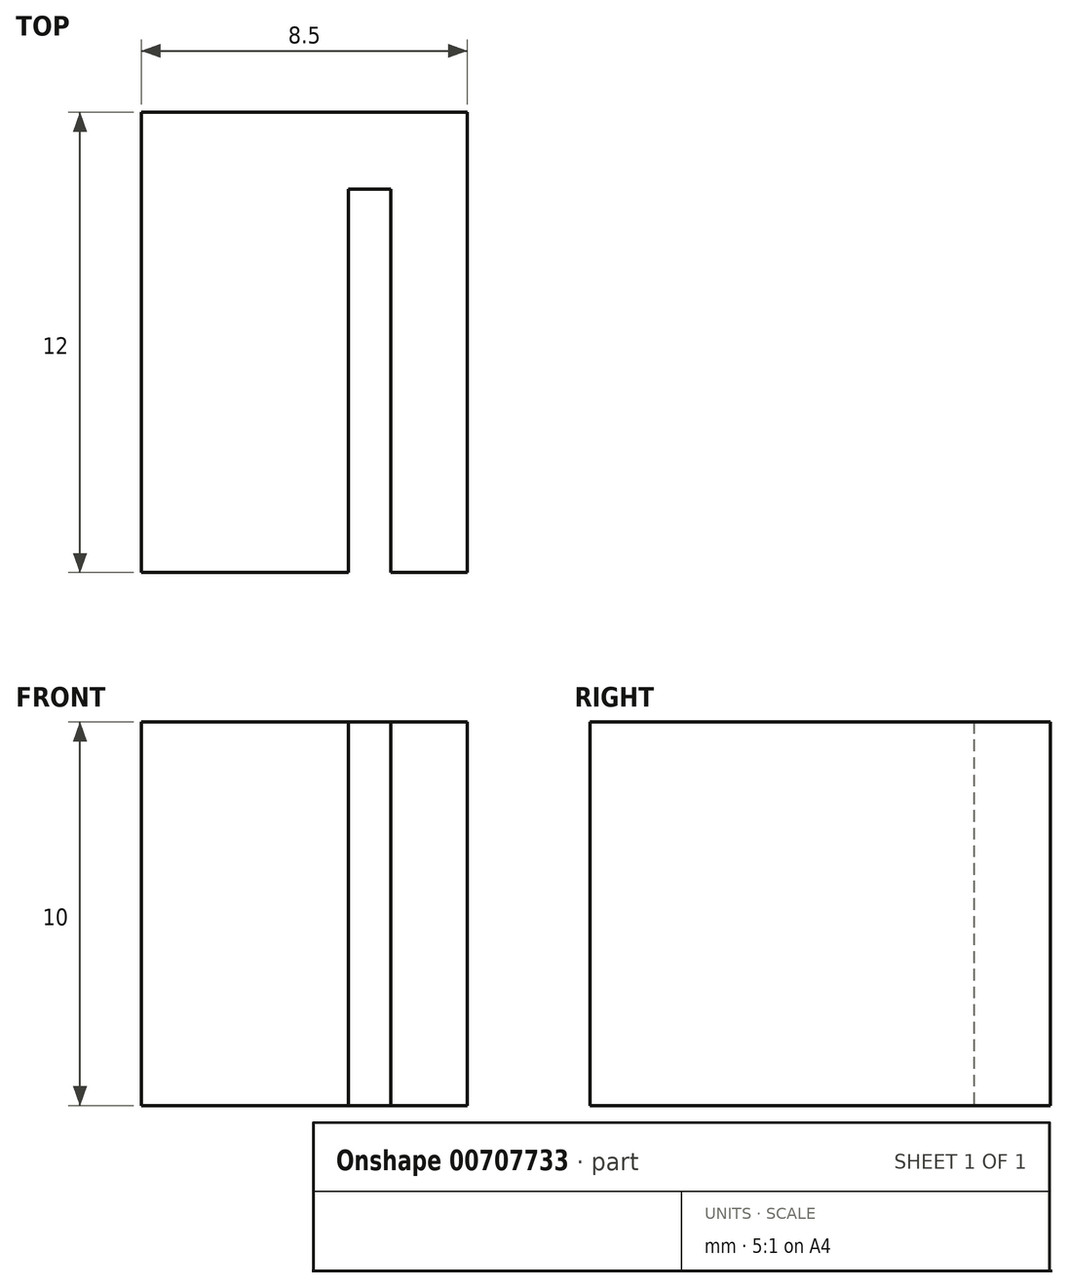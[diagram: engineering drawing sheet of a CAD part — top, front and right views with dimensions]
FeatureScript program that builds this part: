
annotation { "Feature Type Name" : "Feature", "Feature Type Description" : "" }
export const myFeature = defineFeature(function(context is Context, id is Id, definition is map)
    precondition{}
    {
        {
            var Q0;
            Q0=qCreatedBy(makeId("Top.planeOp"),FACE);
            var sketch = newSketch(context, id + "F0", { "sketchPlane" : qUnion([Q0])});
            skLineSegment(sketch, "E0.bottom", {"start": v(0, 0) * mm, "end": v(5.4, 0) * mm});
            skLineSegment(sketch, "E0.top", {"start": v(0, 12) * mm, "end": v(8.5, 12) * mm});
            skLineSegment(sketch, "E0.left", {"start": v(0, 0) * mm, "end": v(0, 12) * mm});
            skLineSegment(sketch, "E0.right", {"start": v(8.5, 0) * mm, "end": v(8.5, 12) * mm});
            skLineSegment(sketch, "E1.top", {"start": v(5.4, 10) * mm, "end": v(6.5, 10) * mm});
            skLineSegment(sketch, "E1.left", {"start": v(5.4, 0) * mm, "end": v(5.4, 10) * mm});
            skLineSegment(sketch, "E1.right", {"start": v(6.5, 0) * mm, "end": v(6.5, 10) * mm});
            skLineSegment(sketch, "E2.trimOffspring", {"start": v(6.5, 0) * mm, "end": v(8.5, 0) * mm});
            skSolve(sketch);
        }
        {
            var Q0;
            Q0=qSketchRegion(id+"F0",true);
            extrude(context, id + "F1", {"entities" : qUnion([Q0]), "depth" : 10 * mm, "offsetDistance" : 25 * mm});
        }
    });
